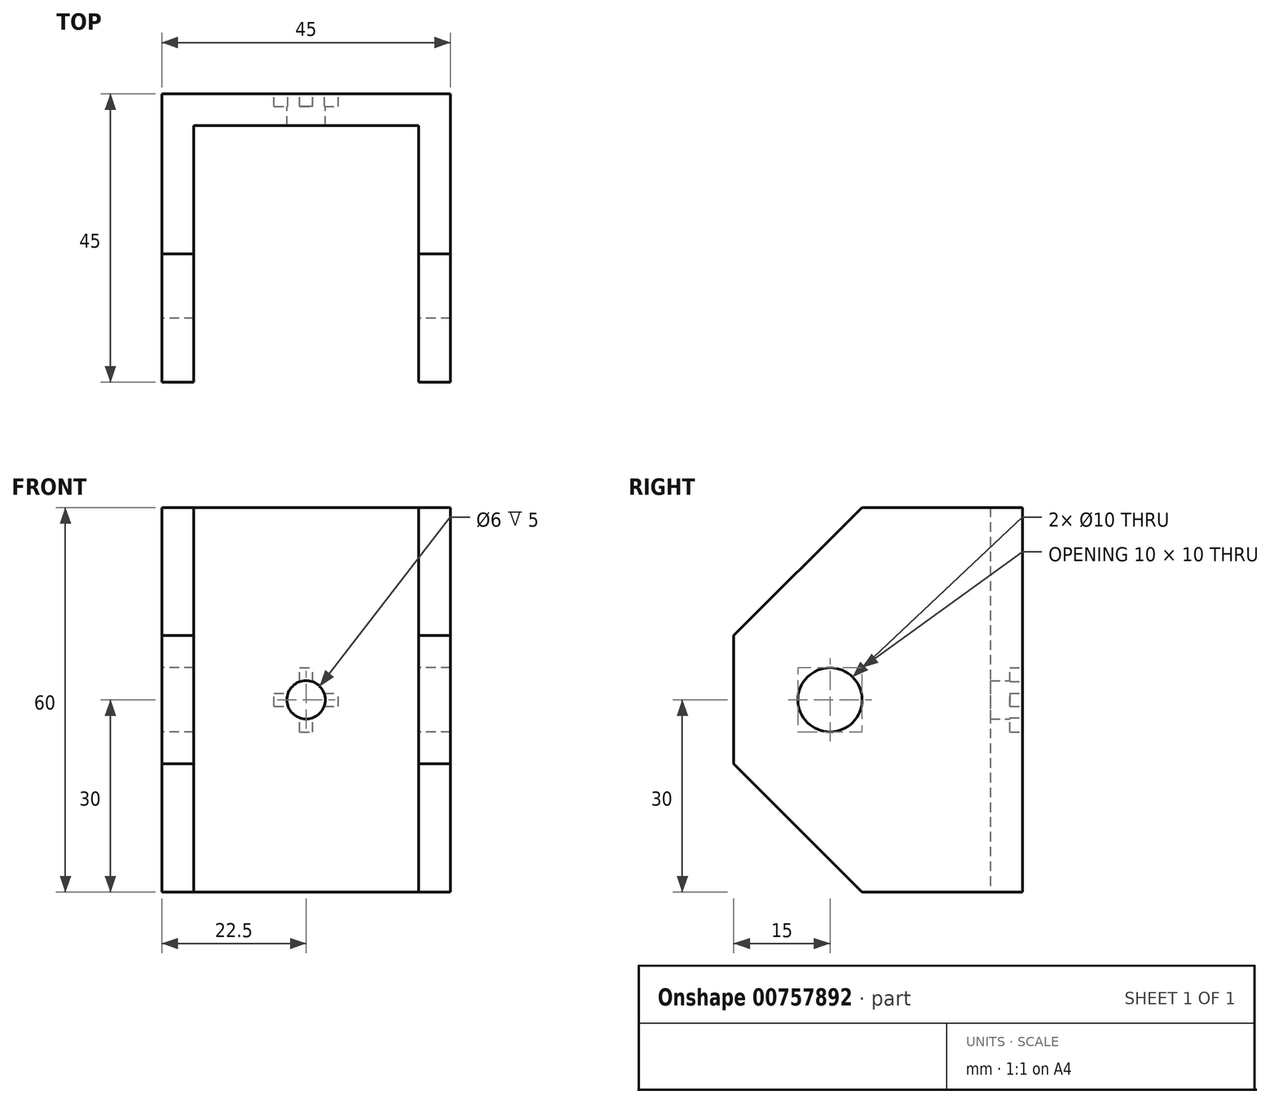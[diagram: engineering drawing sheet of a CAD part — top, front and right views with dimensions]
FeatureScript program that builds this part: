
annotation { "Feature Type Name" : "Feature", "Feature Type Description" : "" }
export const myFeature = defineFeature(function(context is Context, id is Id, definition is map)
    precondition{}
    {
        {
            var Q0;
            Q0=qCreatedBy(makeId("Front.planeOp"),FACE);
            var sketch = newSketch(context, id + "F0", { "sketchPlane" : qUnion([Q0])});
            skLineSegment(sketch, "E0.bottom", {"start": v(22.5, -30) * mm, "end": v(-22.5, -30) * mm});
            skLineSegment(sketch, "E0.top", {"start": v(22.5, 30) * mm, "end": v(-22.5, 30) * mm});
            skLineSegment(sketch, "E0.left", {"start": v(22.5, -30) * mm, "end": v(22.5, 30) * mm});
            skLineSegment(sketch, "E0.right", {"start": v(-22.5, -30) * mm, "end": v(-22.5, 30) * mm});
            skPoint(sketch, "E0.middle", {"position": v(0, 0) * mm});
            skSolve(sketch);
        }
        {
            var Q0;
            Q0 = qSketchRegion(id + "F0", true);
            extrude(context, id + "F1", {"entities" : qUnion([Q0]), "depth" : 5 * mm, "offsetDistance" : 25 * mm});
        }
        {
            var Q0;
            Q0=makeQuery(id+"F1.opExtrude","CAP_FACE",FACE,{"disambiguationData":[OSD([sQuery(id+"F0.wireOp",EDGE,"E0.bottom"),sQuery(id+"F0.wireOp",EDGE,"E0.top"),sQuery(id+"F0.wireOp",EDGE,"E0.left"),sQuery(id+"F0.wireOp",EDGE,"E0.right")])],"isStart":false});
            var sketch = newSketch(context, id + "F2", { "sketchPlane" : qUnion([Q0])});
            skLineSegment(sketch, "E1.bottom", {"start": v(-22.5, 30) * mm, "end": v(-17.5, 30) * mm});
            skLineSegment(sketch, "E1.top", {"start": v(-22.5, -30) * mm, "end": v(-17.5, -30) * mm});
            skLineSegment(sketch, "E1.left", {"start": v(-22.5, 30) * mm, "end": v(-22.5, -30) * mm});
            skLineSegment(sketch, "E1.right", {"start": v(-17.5, 30) * mm, "end": v(-17.5, -30) * mm});
            skLineSegment(sketch, "E2.MirrorCS", {"start": v(22.5, 30) * mm, "end": v(17.5, 30) * mm});
            skLineSegment(sketch, "E3.MirrorCS", {"start": v(22.5, -30) * mm, "end": v(17.5, -30) * mm});
            skLineSegment(sketch, "E4.MirrorCS", {"start": v(22.5, 30) * mm, "end": v(22.5, -30) * mm});
            skLineSegment(sketch, "E5.MirrorCS", {"start": v(17.5, 30) * mm, "end": v(17.5, -30) * mm});
            skSolve(sketch);
        }
        {
            var Q0;
            Q0=makeQuery(id+"F2.imprint","IMPRINT",FACE,{"disambiguationData":[TD([[makeQuery(id+"F2.imprint","IMPRINT",EDGE,{"derivedFrom":sQuery(id+"F2.wireOp",EDGE,"E1.bottom")}),1.0]])]});
            var Q1;
            Q1=makeQuery(id+"F2.imprint","IMPRINT",FACE,{"disambiguationData":[TD([[makeQuery(id+"F2.imprint","IMPRINT",EDGE,{"derivedFrom":sQuery(id+"F2.wireOp",EDGE,"E2.MirrorCS")}),1.0]])]});
            extrude(context, id + "F3", {"entities" : qUnion([Q0, Q1]), "operationType" : NewBodyOperationType.ADD, "depth" : 40 * mm, "offsetDistance" : 25 * mm});
        }
        {
            var Q0;
            Q0=makeQuery(id+"F3.opExtrude","CAP_EDGE",EDGE,{"disambiguationData":[OSD([sQuery(id+"F2.wireOp",EDGE,"E2.MirrorCS")])],"isStart":false});
            var Q1;
            Q1=makeQuery(id+"F3.opExtrude","CAP_EDGE",EDGE,{"disambiguationData":[OSD([sQuery(id+"F2.wireOp",EDGE,"E1.bottom")])],"isStart":false});
            var Q2;
            Q2=makeQuery(id+"F3.opExtrude","CAP_EDGE",EDGE,{"disambiguationData":[OSD([sQuery(id+"F2.wireOp",EDGE,"E3.MirrorCS")])],"isStart":false});
            var Q3;
            Q3=makeQuery(id+"F3.opExtrude","CAP_EDGE",EDGE,{"disambiguationData":[OSD([sQuery(id+"F2.wireOp",EDGE,"E1.top")])],"isStart":false});
            chamfer(context, id + "F4", {"entities" : qUnion([Q0, Q1, Q2, Q3]), "chamferType" : ChamferType.TWO_OFFSETS, "width1" : 20 * mm, "oppositeDirection" : true, "width2" : 20 * mm, "tangentPropagation" : true});
        }
        {
            var Q0;
            Q0=makeQuery(id+"F3.boolean.opBoolean","MERGE",FACE,{"derivedFrom":[makeQuery(id+"F1.opExtrude","SWEPT_FACE",FACE,{"disambiguationData":[OSD([sQuery(id+"F0.wireOp",EDGE,"E0.right")])]}),makeQuery(id+"F3.opExtrude","SWEPT_FACE",FACE,{"disambiguationData":[OSD([sQuery(id+"F2.wireOp",EDGE,"E1.left")])]})]});
            var sketch = newSketch(context, id + "F5", { "sketchPlane" : qUnion([Q0])});
            skCircle(sketch, "E6", {"center": v(30, 0) * mm, "radius": 5 * mm});
            skSolve(sketch);
        }
        {
            var Q0;
            Q0=makeQuery(id+"F5.imprint","IMPRINT",FACE,{"disambiguationData":[TD([[makeQuery(id+"F5.imprint","IMPRINT",EDGE,{"derivedFrom":sQuery(id+"F5.wireOp",EDGE,"E6")}),1.0]])]});
            extrude(context, id + "F6", {"entities" : qUnion([Q0]), "operationType" : NewBodyOperationType.REMOVE, "oppositeDirection" : true, "depth" : 50 * mm, "offsetDistance" : 25 * mm});
        }
        {
            var Q0;
            Q0=makeQuery(id+"F1.opExtrude","CAP_FACE",FACE,{"disambiguationData":[OSD([sQuery(id+"F0.wireOp",EDGE,"E0.bottom"),sQuery(id+"F0.wireOp",EDGE,"E0.top"),sQuery(id+"F0.wireOp",EDGE,"E0.left"),sQuery(id+"F0.wireOp",EDGE,"E0.right")])],"isStart":false});
            var sketch = newSketch(context, id + "F7", { "sketchPlane" : qUnion([Q0])});
            skPoint(sketch, "E7", {"position": v(0, 0) * mm});
            skSolve(sketch);
        }
        {
            var Q0;
            Q0=sQuery(id+"F7.wireOp",VERTEX,"E7");
            var Q1;
            Q1=makeQuery(id+"F1.opExtrude","SWEPT_BODY",BODY,{"disambiguationData":[OSD([sQuery(id+"F0.wireOp",EDGE,"E0.bottom"),sQuery(id+"F0.wireOp",EDGE,"E0.top"),sQuery(id+"F0.wireOp",EDGE,"E0.left"),sQuery(id+"F0.wireOp",EDGE,"E0.right")])]});
            hole(context, id + "F8", {"style" : HoleStyle.SIMPLE, "endStyle" : HoleEndStyle.BLIND, "holeDiameter" : 6 * mm, "majorDiameter" : 5 * mm, "holeDepth" : 20 * mm, "isTappedThrough" : true, "tappedDepth" : 12 * mm, "tapClearance" : 3, "startFromSketch" : true, "locations" : qUnion([Q0]), "scope" : qUnion([Q1])});
        }
        {
            var Q0;
            Q0=makeQuery(id+"F1.opExtrude","CAP_FACE",FACE,{"disambiguationData":[OSD([sQuery(id+"F0.wireOp",EDGE,"E0.bottom"),sQuery(id+"F0.wireOp",EDGE,"E0.top"),sQuery(id+"F0.wireOp",EDGE,"E0.left"),sQuery(id+"F0.wireOp",EDGE,"E0.right")])],"isStart":true});
            var sketch = newSketch(context, id + "F9", { "sketchPlane" : qUnion([Q0])});
            skLineSegment(sketch, "E8.bottom", {"start": v(5, -1) * mm, "end": v(-5, -1) * mm});
            skLineSegment(sketch, "E8.top", {"start": v(5, 1) * mm, "end": v(-5, 1) * mm});
            skLineSegment(sketch, "E8.left", {"start": v(5, -1) * mm, "end": v(5, 1) * mm});
            skLineSegment(sketch, "E8.right", {"start": v(-5, -1) * mm, "end": v(-5, 1) * mm});
            skPoint(sketch, "E8.middle", {"position": v(0, 0) * mm});
            skLineSegment(sketch, "E9.bottom", {"start": v(1, -5) * mm, "end": v(-1, -5) * mm});
            skLineSegment(sketch, "E9.top", {"start": v(1, 5) * mm, "end": v(-1, 5) * mm});
            skLineSegment(sketch, "E9.left", {"start": v(1, -5) * mm, "end": v(1, 5) * mm});
            skLineSegment(sketch, "E9.right", {"start": v(-1, -5) * mm, "end": v(-1, 5) * mm});
            skCircle(sketch, "E10", {"center": v(0.13, 0) * mm, "radius": 4 * mm});
            skSolve(sketch);
        }
        {
            var Q0;
            {var subQ0=sQuery(id+"F9.wireOp",EDGE,"E8.right");Q0=makeQuery(id+"F9.imprint","IMPRINT",FACE,{"disambiguationData":[TD([[makeQuery(id+"F9.imprint","IMPRINT",EDGE,{"derivedFrom":subQ0}),-1.0]])]});}
            var Q1;
            {var subQ0=sQuery(id+"F9.wireOp",EDGE,"E9.top");Q1=makeQuery(id+"F9.imprint","IMPRINT",FACE,{"disambiguationData":[TD([[makeQuery(id+"F9.imprint","IMPRINT",EDGE,{"derivedFrom":subQ0}),1.0]])]});}
            var Q2;
            {var subQ0=sQuery(id+"F9.wireOp",EDGE,"E8.left");Q2=makeQuery(id+"F9.imprint","IMPRINT",FACE,{"disambiguationData":[TD([[makeQuery(id+"F9.imprint","IMPRINT",EDGE,{"derivedFrom":subQ0}),1.0]])]});}
            var Q3;
            {var subQ0=sQuery(id+"F9.wireOp",EDGE,"E9.bottom");Q3=makeQuery(id+"F9.imprint","IMPRINT",FACE,{"disambiguationData":[TD([[makeQuery(id+"F9.imprint","IMPRINT",EDGE,{"derivedFrom":subQ0}),-1.0]])]});}
            extrude(context, id + "F10", {"entities" : qUnion([Q0, Q1, Q2, Q3]), "operationType" : NewBodyOperationType.REMOVE, "oppositeDirection" : true, "depth" : 2 * mm, "offsetDistance" : 25 * mm});
        }
        {
            var Q0;
            {var subQ0=sQuery(id+"F9.wireOp",EDGE,"E10");var subQ1=sQuery(id+"F9.wireOp",EDGE,"E8.bottom");var subQ2=makeQuery(id+"F9.imprint","INTERSECT",VERTEX,{"disambiguationData":[OD(0.0)],"derivedFrom":[subQ1,subQ0]});Q0=makeQuery(id+"F9.imprint","IMPRINT",FACE,{"disambiguationData":[TD([[makeQuery(id+"F9.imprint","IMPRINT",EDGE,{"disambiguationData":[TD([[subQ2,-1.0]])],"derivedFrom":subQ0}),1.0]])]});}
            var Q1;
            {var subQ0=sQuery(id+"F9.wireOp",EDGE,"E10");var subQ1=sQuery(id+"F9.wireOp",EDGE,"E8.bottom");var subQ2=makeQuery(id+"F9.imprint","INTERSECT",VERTEX,{"disambiguationData":[OD(1.0)],"derivedFrom":[subQ1,subQ0]});Q1=makeQuery(id+"F9.imprint","IMPRINT",FACE,{"disambiguationData":[TD([[makeQuery(id+"F9.imprint","IMPRINT",EDGE,{"disambiguationData":[TD([[subQ2,1.0]])],"derivedFrom":subQ0}),1.0]])]});}
            var Q2;
            {var subQ0=sQuery(id+"F9.wireOp",EDGE,"E10");var subQ1=sQuery(id+"F9.wireOp",EDGE,"E9.left");var subQ2=makeQuery(id+"F9.imprint","INTERSECT",VERTEX,{"disambiguationData":[OD(1.0)],"derivedFrom":[subQ1,subQ0]});Q2=makeQuery(id+"F9.imprint","IMPRINT",FACE,{"disambiguationData":[TD([[makeQuery(id+"F9.imprint","IMPRINT",EDGE,{"disambiguationData":[TD([[subQ2,-1.0]])],"derivedFrom":subQ0}),1.0]])]});}
            var Q3;
            {var subQ0=sQuery(id+"F9.wireOp",EDGE,"E10");var subQ1=sQuery(id+"F9.wireOp",EDGE,"E9.left");var subQ2=makeQuery(id+"F9.imprint","INTERSECT",VERTEX,{"disambiguationData":[OD(0.0)],"derivedFrom":[subQ1,subQ0]});Q3=makeQuery(id+"F9.imprint","IMPRINT",FACE,{"disambiguationData":[TD([[makeQuery(id+"F9.imprint","IMPRINT",EDGE,{"disambiguationData":[TD([[subQ2,1.0]])],"derivedFrom":subQ0}),1.0]])]});}
            extrude(context, id + "F11", {"entities" : qUnion([Q0, Q1, Q2, Q3]), "operationType" : NewBodyOperationType.REMOVE, "oppositeDirection" : true, "depth" : 2 * mm, "offsetDistance" : 25 * mm});
        }
    });
